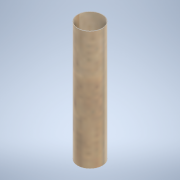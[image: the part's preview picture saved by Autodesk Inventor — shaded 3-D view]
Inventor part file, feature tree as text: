
AUTODESK INVENTOR PART (.ipt)
format: ipt  version: 2021 (Build 250183000, 183)  size: 109,568 bytes
history: native  units: mm
features: revolve x1, sketch x1
ambient origin geometry x8: Origin, YZ Plane, XZ Plane, XY Plane, X Axis, Y Axis, Z Axis, Center Point
bodies: Solid1 (feature_tree)
feature tree (2):
  revolve  "Revolution1"  [1 undecoded]
  sketch  "Sketch1"  dims[d0=15.0mm d1=15.5mm d2=150.0mm d3=90.0deg]
note: 1 required parameter value undecoded (feature->parameter linkage not recoverable at this tier; creation-order binding heuristic only, values carry confidence <= 0.55)
